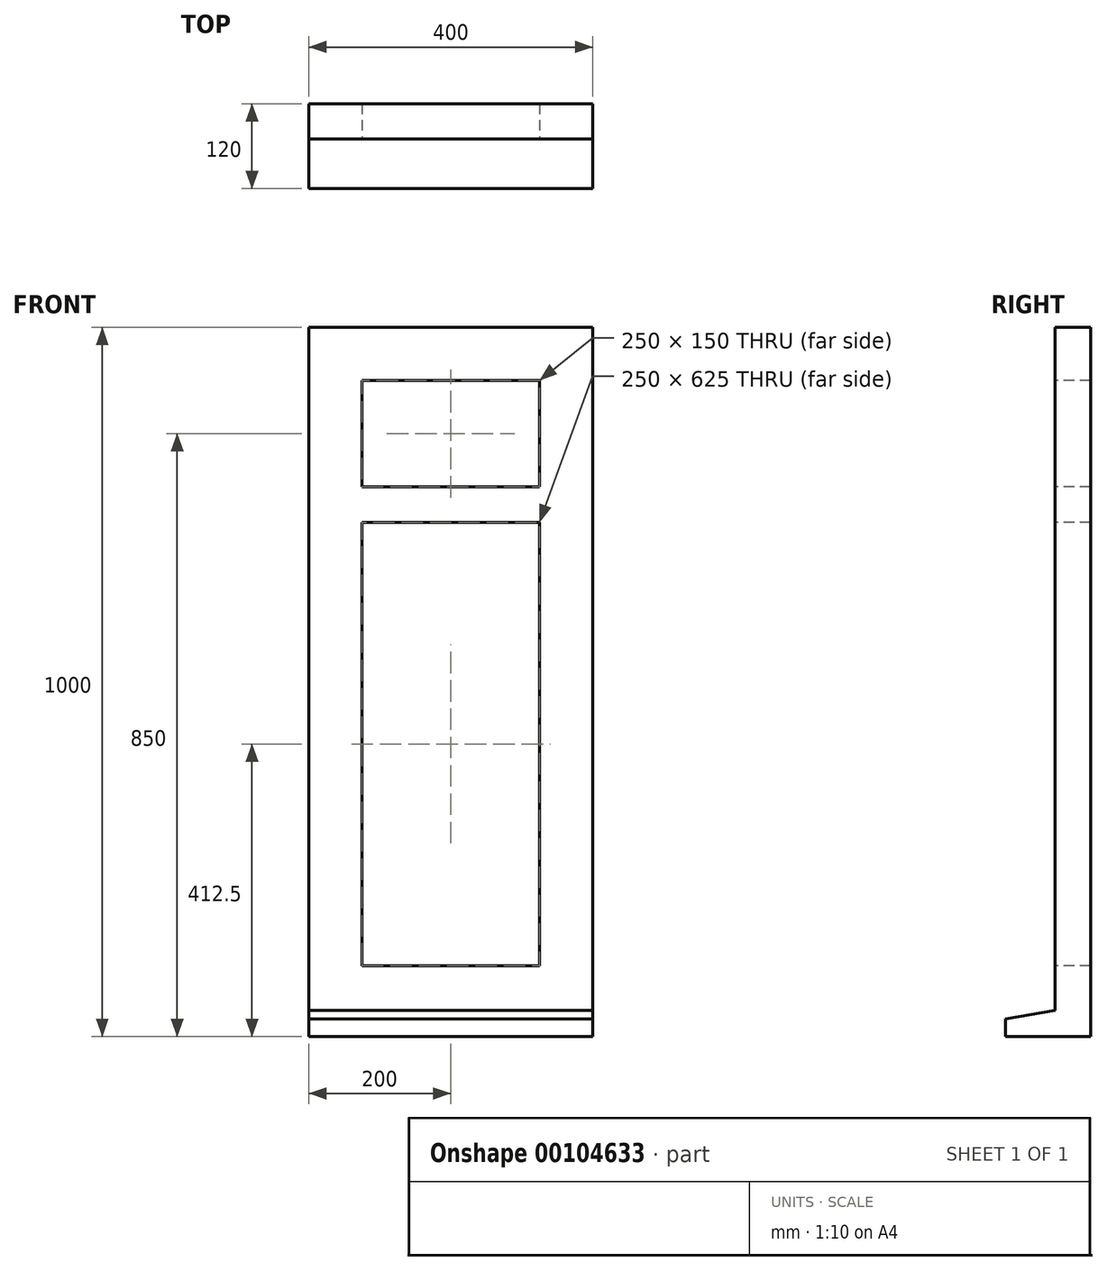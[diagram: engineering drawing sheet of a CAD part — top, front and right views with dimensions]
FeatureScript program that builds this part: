
annotation { "Feature Type Name" : "Feature", "Feature Type Description" : "" }
export const myFeature = defineFeature(function(context is Context, id is Id, definition is map)
    precondition{}
    {
        {
            var Q0;
            Q0=qCreatedBy(makeId("Front.planeOp"),FACE);
            var sketch = newSketch(context, id + "F0", { "sketchPlane" : qUnion([Q0])});
            skLineSegment(sketch, "E0.bottom", {"start": v(0, 0) * mm, "end": v(400, 0) * mm});
            skLineSegment(sketch, "E0.top", {"start": v(0, -1000) * mm, "end": v(400, -1000) * mm});
            skLineSegment(sketch, "E0.left", {"start": v(0, 0) * mm, "end": v(0, -1000) * mm});
            skLineSegment(sketch, "E0.right", {"start": v(400, 0) * mm, "end": v(400, -1000) * mm});
            skLineSegment(sketch, "E1.bottom", {"start": v(75, -275) * mm, "end": v(325, -275) * mm});
            skLineSegment(sketch, "E1.top", {"start": v(75, -900) * mm, "end": v(325, -900) * mm});
            skLineSegment(sketch, "E1.left", {"start": v(75, -275) * mm, "end": v(75, -900) * mm});
            skLineSegment(sketch, "E1.right", {"start": v(325, -275) * mm, "end": v(325, -900) * mm});
            skLineSegment(sketch, "E2.bottom", {"start": v(75, -75) * mm, "end": v(325, -75) * mm});
            skLineSegment(sketch, "E2.top", {"start": v(75, -225) * mm, "end": v(325, -225) * mm});
            skLineSegment(sketch, "E2.left", {"start": v(75, -75) * mm, "end": v(75, -225) * mm});
            skLineSegment(sketch, "E2.right", {"start": v(325, -75) * mm, "end": v(325, -225) * mm});
            skPoint(sketch, "E3.firstSnap0", {"position": v(200, -225) * mm});
            skSolve(sketch);
        }
        {
            var Q0;
            Q0=qSketchRegion(id+"F0",true);
            extrude(context, id + "F1", {"entities" : qUnion([Q0]), "oppositeDirection" : true, "depth" : 50 * mm});
        }
        {
            var Q0;
            Q0=makeQuery(id+"F1.opExtrude","SWEPT_FACE",FACE,{"disambiguationData":[OSD([sQuery(id+"F0.wireOp",EDGE,"E0.right")])]});
            var sketch = newSketch(context, id + "F2", { "sketchPlane" : qUnion([Q0])});
            skLineSegment(sketch, "E4", {"start": v(0, -1000) * mm, "end": v(-70, -1000) * mm});
            skLineSegment(sketch, "E5", {"start": v(0, -962.66) * mm, "end": v(-70, -975) * mm});
            skLineSegment(sketch, "E6", {"start": v(-70, -975) * mm, "end": v(-70, -1000) * mm});
            skLineSegment(sketch, "E7", {"start": v(0, -1000) * mm, "end": v(0, -962.66) * mm});
            skSolve(sketch);
        }
        {
            var Q0;
            Q0=qSketchRegion(id+"F2",true);
            extrude(context, id + "F3", {"entities" : qUnion([Q0]), "operationType" : NewBodyOperationType.ADD, "oppositeDirection" : true, "depth" : 400 * mm});
        }
    });
